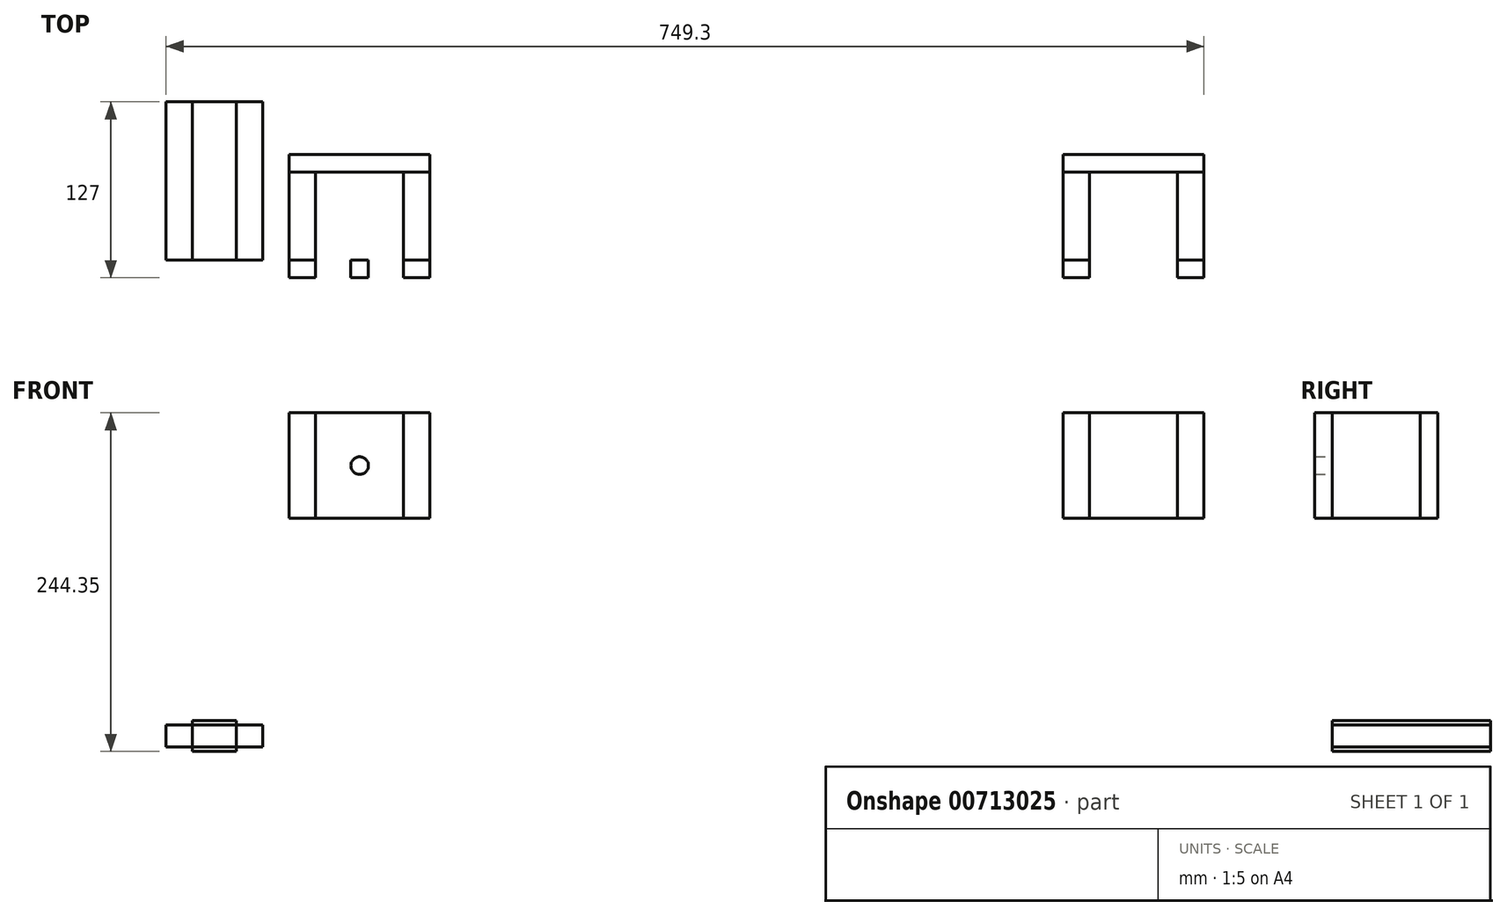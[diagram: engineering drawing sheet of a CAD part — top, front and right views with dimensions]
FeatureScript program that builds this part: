
annotation { "Feature Type Name" : "Feature", "Feature Type Description" : "" }
export const myFeature = defineFeature(function(context is Context, id is Id, definition is map)
    precondition{}
    {
        {
            assignVariable(context, id + "F0", {"name" : "smallWoodDim", "anyValue" : 0.75});
        }
        {
            assignVariable(context, id + "F1", {"name" : "boxWidth", "anyValue" : 2.75 * 12});
        }
        {
            assignVariable(context, id + "F2", {"name" : "boxHeight", "anyValue" : 16});
        }
        {
            var Q0;
            Q0=qCreatedBy(makeId("Top.planeOp"),FACE);
            var sketch = newSketch(context, id + "F3", { "sketchPlane" : qUnion([Q0])});
            skLineSegment(sketch, "E0.bottom", {"start": v(0, 0) * mm, "end": v(19.05, 0) * mm});
            skLineSegment(sketch, "E0.top", {"start": v(0, -114.3) * mm, "end": v(19.05, -114.3) * mm});
            skLineSegment(sketch, "E0.left", {"start": v(0, 0) * mm, "end": v(0, -114.3) * mm});
            skLineSegment(sketch, "E0.right", {"start": v(19.05, 0) * mm, "end": v(19.05, -114.3) * mm});
            skSolve(sketch);
        }
        {
            var Q0;
            Q0 = qSketchRegion(id + "F3", true);
            extrude(context, id + "F4", {"entities" : qUnion([Q0]), "depth" : (getVariable(context, 'boxHeight')) * mm, "offsetDistance" : 25.4 * mm});
        }
        {
            var Q0;
            Q0=makeQuery(id+"F4.opExtrude","SWEPT_FACE",FACE,{"disambiguationData":[OSD([sQuery(id+"F3.wireOp",EDGE,"E0.right")])]});
            var sketch = newSketch(context, id + "F5", { "sketchPlane" : qUnion([Q0])});
            skLineSegment(sketch, "E1.bottom", {"start": v(0, 0) * mm, "end": v(-114.3, 0) * mm});
            skLineSegment(sketch, "E1.top", {"start": v(0, 19.05) * mm, "end": v(-114.3, 19.05) * mm});
            skLineSegment(sketch, "E1.left", {"start": v(0, 0) * mm, "end": v(0, 19.05) * mm});
            skLineSegment(sketch, "E1.right", {"start": v(-114.3, 0) * mm, "end": v(-114.3, 19.05) * mm});
            skSolve(sketch);
        }
        {
            var Q0;
            Q0 = qSketchRegion(id + "F5", true);
            extrude(context, id + "F6", {"entities" : qUnion([Q0]), "depth" : (getVariable(context, 'boxWidth') - 2 * getVariable(context, 'smallWoodDim')) * mm, "offsetDistance" : 25.4 * mm});
        }
        {
            var Q0;
            Q0=makeQuery(id+"F4.opExtrude","SWEPT_EDGE",EDGE,{"disambiguationData":[OSD([sQuery(id+"F3.wireOp",EDGE,"E0.top"),sQuery(id+"F3.wireOp",EDGE,"E0.left")])]});
            cPoint(context, id + "F7", {"entities" : qUnion([Q0]), "parameter" : 0.5});
        }
        {
            var Q0;
            Q0=makeQuery(id+"F4.opExtrude","SWEPT_EDGE",EDGE,{"disambiguationData":[OSD([sQuery(id+"F3.wireOp",EDGE,"E0.top"),sQuery(id+"F3.wireOp",EDGE,"E0.right")])]});
            cPoint(context, id + "F8", {"entities" : qUnion([Q0]), "parameter" : 0.5});
        }
        {
            var Q0;
            Q0=makeQuery(id+"F4.opExtrude","SWEPT_EDGE",EDGE,{"disambiguationData":[OSD([sQuery(id+"F3.wireOp",EDGE,"E0.bottom"),sQuery(id+"F3.wireOp",EDGE,"E0.left")])]});
            cPoint(context, id + "F9", {"entities" : qUnion([Q0]), "parameter" : 0.5});
        }
        {
            var Q0;
            Q0 = qCreatedBy(id + "F7" ,VERTEX);
            var Q1;
            Q1 = qCreatedBy(id + "F8" ,VERTEX);
            var Q2;
            Q2 = qCreatedBy(id + "F9" ,VERTEX);
            cPlane(context, id + "F10", {"entities" : qUnion([Q0, Q1, Q2]), "cplaneType" : CPlaneType.THREE_POINT, "offset" : 25.4 * mm, "width" : 152.4 * mm, "height" : 152.4 * mm});
        }
        {
            var Q0;
            Q0=makeQuery(id+"F6.opExtrude","SWEPT_EDGE",EDGE,{"disambiguationData":[OSD([sQuery(id+"F5.wireOp",EDGE,"E1.bottom"),sQuery(id+"F5.wireOp",EDGE,"E1.right")])]});
            cPoint(context, id + "F11", {"entities" : qUnion([Q0]), "parameter" : 0.5});
        }
        {
            var Q0;
            Q0=makeQuery(id+"F6.opExtrude","SWEPT_EDGE",EDGE,{"disambiguationData":[OSD([sQuery(id+"F3.wireOp",EDGE,"E0.top"),sQuery(id+"F3.wireOp",EDGE,"E0.right"),sQuery(id+"F5.wireOp",EDGE,"E1.top"),sQuery(id+"F5.wireOp",EDGE,"E1.right")])]});
            cPoint(context, id + "F12", {"entities" : qUnion([Q0]), "parameter" : 0.5});
        }
        {
            var Q0;
            Q0=makeQuery(id+"F6.opExtrude","SWEPT_EDGE",EDGE,{"disambiguationData":[OSD([sQuery(id+"F3.wireOp",EDGE,"E0.bottom"),sQuery(id+"F3.wireOp",EDGE,"E0.right"),sQuery(id+"F5.wireOp",EDGE,"E1.top"),sQuery(id+"F5.wireOp",EDGE,"E1.left")])]});
            cPoint(context, id + "F13", {"entities" : qUnion([Q0]), "parameter" : 0.5});
        }
        {
            var Q0;
            Q0 = qCreatedBy(id + "F11" ,VERTEX);
            var Q1;
            Q1 = qCreatedBy(id + "F12" ,VERTEX);
            var Q2;
            Q2 = qCreatedBy(id + "F13" ,VERTEX);
            cPlane(context, id + "F14", {"entities" : qUnion([Q0, Q1, Q2]), "cplaneType" : CPlaneType.THREE_POINT, "offset" : 25.4 * mm, "width" : 152.4 * mm, "height" : 152.4 * mm});
        }
        {
            var Q0;
            Q0=makeQuery(id+"F6.opExtrude","SWEPT_BODY",BODY,{"disambiguationData":[OSD([sQuery(id+"F5.wireOp",EDGE,"E1.bottom"),sQuery(id+"F5.wireOp",EDGE,"E1.top"),sQuery(id+"F5.wireOp",EDGE,"E1.left"),sQuery(id+"F5.wireOp",EDGE,"E1.right")])]});
            var Q1;
            Q1=qCreatedBy(id+"F10.planeOp",FACE);
            mirror(context, id + "F15", {"entities" : qUnion([Q0]), "mirrorPlane" : qUnion([Q1])});
        }
        {
            var Q0;
            Q0=makeQuery(id+"F4.opExtrude","SWEPT_BODY",BODY,{"disambiguationData":[OSD([sQuery(id+"F3.wireOp",EDGE,"E0.bottom"),sQuery(id+"F3.wireOp",EDGE,"E0.top"),sQuery(id+"F3.wireOp",EDGE,"E0.left"),sQuery(id+"F3.wireOp",EDGE,"E0.right")])]});
            var Q1;
            Q1=qCreatedBy(id+"F14.planeOp",FACE);
            mirror(context, id + "F16", {"entities" : qUnion([Q0]), "mirrorPlane" : qUnion([Q1])});
        }
        {
            var Q0;
            Q0=makeQuery(id+"F4.opExtrude","SWEPT_FACE",FACE,{"disambiguationData":[OSD([sQuery(id+"F3.wireOp",EDGE,"E0.top")])]});
            var sketch = newSketch(context, id + "F17", { "sketchPlane" : qUnion([Q0])});
            skLineSegment(sketch, "E2.bottom", {"start": v(0, 406.4) * mm, "end": v(838.2, 406.4) * mm});
            skLineSegment(sketch, "E2.top", {"start": v(0, 0) * mm, "end": v(838.2, 0) * mm});
            skLineSegment(sketch, "E2.left", {"start": v(0, 406.4) * mm, "end": v(0, 0) * mm});
            skLineSegment(sketch, "E2.right", {"start": v(838.2, 406.4) * mm, "end": v(838.2, 0) * mm});
            skSolve(sketch);
        }
        {
            var Q0;
            Q0 = qSketchRegion(id + "F17", true);
            extrude(context, id + "F18", {"entities" : qUnion([Q0]), "depth" : 12.7 * mm, "offsetDistance" : 25.4 * mm});
        }
        {
            var Q0;
            Q0=makeQuery(id+"F18.opExtrude","CAP_FACE",FACE,{"disambiguationData":[OSD([sQuery(id+"F17.wireOp",EDGE,"E2.bottom"),sQuery(id+"F17.wireOp",EDGE,"E2.top"),sQuery(id+"F17.wireOp",EDGE,"E2.left"),sQuery(id+"F17.wireOp",EDGE,"E2.right")])],"isStart":true});
            var sketch = newSketch(context, id + "F19", { "sketchPlane" : qUnion([Q0])});
            skPoint(sketch, "E3", {"position": v(-419.1, 203.2) * mm});
            skPoint(sketch, "E3.positionSnap0", {"position": v(0, 203.2) * mm});
            skPoint(sketch, "E3.positionSnap1", {"position": v(-419.1, 0) * mm});
            skCircle(sketch, "E4", {"center": v(-698.5, 203.2) * mm, "radius": 41.28 * mm, "construction": true});
            skLineSegment(sketch, "E5", {"start": v(-698.5, 203.2) * mm, "end": v(-139.7, 203.2) * mm, "construction": true});
            skLineSegment(sketch, "E6.bottom", {"start": v(-647.7, 241.3) * mm, "end": v(-666.75, 241.3) * mm});
            skLineSegment(sketch, "E6.top", {"start": v(-647.7, 165.1) * mm, "end": v(-666.75, 165.1) * mm});
            skLineSegment(sketch, "E6.left", {"start": v(-647.7, 241.3) * mm, "end": v(-647.7, 165.1) * mm});
            skLineSegment(sketch, "E6.right", {"start": v(-666.75, 241.3) * mm, "end": v(-666.75, 165.1) * mm});
            skPoint(sketch, "E6.middle", {"position": v(-657.22, 203.2) * mm});
            skLineSegment(sketch, "E7.bottom", {"start": v(-730.25, 241.3) * mm, "end": v(-749.3, 241.3) * mm});
            skLineSegment(sketch, "E7.top", {"start": v(-730.25, 165.1) * mm, "end": v(-749.3, 165.1) * mm});
            skLineSegment(sketch, "E7.left", {"start": v(-730.25, 241.3) * mm, "end": v(-730.25, 165.1) * mm});
            skLineSegment(sketch, "E7.right", {"start": v(-749.3, 241.3) * mm, "end": v(-749.3, 165.1) * mm});
            skPoint(sketch, "E7.middle", {"position": v(-739.77, 203.2) * mm});
            skLineSegment(sketch, "E8.MirrorCS", {"start": v(-107.95, 241.3) * mm, "end": v(-88.9, 241.3) * mm});
            skLineSegment(sketch, "E9.MirrorCS", {"start": v(-107.95, 165.1) * mm, "end": v(-88.9, 165.1) * mm});
            skLineSegment(sketch, "E10.MirrorCS", {"start": v(-190.5, 241.3) * mm, "end": v(-171.45, 241.3) * mm});
            skLineSegment(sketch, "E11.MirrorCS", {"start": v(-190.5, 165.1) * mm, "end": v(-171.45, 165.1) * mm});
            skLineSegment(sketch, "E12.MirrorCS", {"start": v(-88.9, 241.3) * mm, "end": v(-88.9, 165.1) * mm});
            skLineSegment(sketch, "E13.MirrorCS", {"start": v(-171.45, 241.3) * mm, "end": v(-171.45, 165.1) * mm});
            skLineSegment(sketch, "E14.MirrorCS", {"start": v(-190.5, 241.3) * mm, "end": v(-190.5, 165.1) * mm});
            skLineSegment(sketch, "E15.MirrorCS", {"start": v(-107.95, 241.3) * mm, "end": v(-107.95, 165.1) * mm});
            skPoint(sketch, "E16.MirrorP", {"position": v(-98.43, 203.2) * mm});
            skLineSegment(sketch, "E17.MirrorCS", {"start": v(-139.7, 203.2) * mm, "end": v(-698.5, 203.2) * mm, "construction": true});
            skCircle(sketch, "E18.MirrorC", {"center": v(-139.7, 203.2) * mm, "radius": 41.28 * mm, "construction": true});
            skPoint(sketch, "E19.MirrorP", {"position": v(-180.98, 203.2) * mm});
            skCircle(sketch, "E20", {"center": v(-698.5, 203.2) * mm, "radius": 6.35 * mm});
            skCircle(sketch, "E21.MirrorC", {"center": v(-139.7, 203.2) * mm, "radius": 6.35 * mm});
            skSolve(sketch);
        }
        {
            var Q0;
            Q0=makeQuery(id+"F19.imprint","IMPRINT",FACE,{"disambiguationData":[TD([[makeQuery(id+"F19.imprint","IMPRINT",EDGE,{"derivedFrom":sQuery(id+"F19.wireOp",EDGE,"E6.bottom")}),1.0]])]});
            var Q1;
            Q1=makeQuery(id+"F19.imprint","IMPRINT",FACE,{"disambiguationData":[TD([[makeQuery(id+"F19.imprint","IMPRINT",EDGE,{"derivedFrom":sQuery(id+"F19.wireOp",EDGE,"E7.bottom")}),1.0]])]});
            var Q2;
            Q2=makeQuery(id+"F19.imprint","IMPRINT",FACE,{"disambiguationData":[TD([[makeQuery(id+"F19.imprint","IMPRINT",EDGE,{"derivedFrom":sQuery(id+"F19.wireOp",EDGE,"E8.MirrorCS")}),-1.0]])]});
            var Q3;
            Q3=makeQuery(id+"F19.imprint","IMPRINT",FACE,{"disambiguationData":[TD([[makeQuery(id+"F19.imprint","IMPRINT",EDGE,{"derivedFrom":sQuery(id+"F19.wireOp",EDGE,"E10.MirrorCS")}),-1.0]])]});
            extrude(context, id + "F20", {"entities" : qUnion([Q0, Q1, Q2, Q3]), "depth" : 63.5 * mm, "offsetDistance" : 25.4 * mm});
        }
        {
            var Q0;
            Q0=makeQuery(id+"F19.imprint","IMPRINT",FACE,{"disambiguationData":[TD([[makeQuery(id+"F19.imprint","IMPRINT",EDGE,{"derivedFrom":sQuery(id+"F19.wireOp",EDGE,"E21.MirrorC")}),-1.0]])]});
            var Q1;
            Q1=makeQuery(id+"F19.imprint","IMPRINT",FACE,{"disambiguationData":[TD([[makeQuery(id+"F19.imprint","IMPRINT",EDGE,{"derivedFrom":sQuery(id+"F19.wireOp",EDGE,"E20")}),1.0]])]});
            extrude(context, id + "F21", {"entities" : qUnion([Q0, Q1]), "operationType" : NewBodyOperationType.REMOVE, "endBound" : BoundingType.UP_TO_NEXT, "oppositeDirection" : true, "depth" : 25.4 * mm, "offsetDistance" : 25.4 * mm});
        }
        {
            var Q0;
            Q0=makeQuery(id+"F20.opExtrude","CAP_FACE",FACE,{"disambiguationData":[OSD([sQuery(id+"F19.wireOp",EDGE,"E7.bottom"),sQuery(id+"F19.wireOp",EDGE,"E7.top"),sQuery(id+"F19.wireOp",EDGE,"E7.left"),sQuery(id+"F19.wireOp",EDGE,"E7.right")])],"isStart":false});
            var sketch = newSketch(context, id + "F22", { "sketchPlane" : qUnion([Q0])});
            skLineSegment(sketch, "E22.bottom", {"start": v(-749.3, 241.3) * mm, "end": v(-647.7, 241.3) * mm});
            skLineSegment(sketch, "E22.top", {"start": v(-749.3, 165.1) * mm, "end": v(-647.7, 165.1) * mm});
            skLineSegment(sketch, "E22.left", {"start": v(-749.3, 241.3) * mm, "end": v(-749.3, 165.1) * mm});
            skLineSegment(sketch, "E22.right", {"start": v(-647.7, 241.3) * mm, "end": v(-647.7, 165.1) * mm});
            skLineSegment(sketch, "E23.bottom", {"start": v(-190.5, 241.3) * mm, "end": v(-88.9, 241.3) * mm});
            skLineSegment(sketch, "E23.top", {"start": v(-190.5, 165.1) * mm, "end": v(-88.9, 165.1) * mm});
            skLineSegment(sketch, "E23.left", {"start": v(-190.5, 241.3) * mm, "end": v(-190.5, 165.1) * mm});
            skLineSegment(sketch, "E23.right", {"start": v(-88.9, 241.3) * mm, "end": v(-88.9, 165.1) * mm});
            skSolve(sketch);
        }
        {
            var Q0;
            Q0 = qSketchRegion(id + "F22", true);
            extrude(context, id + "F23", {"entities" : qUnion([Q0]), "depth" : 12.7 * mm, "offsetDistance" : 25.4 * mm});
        }
    });
